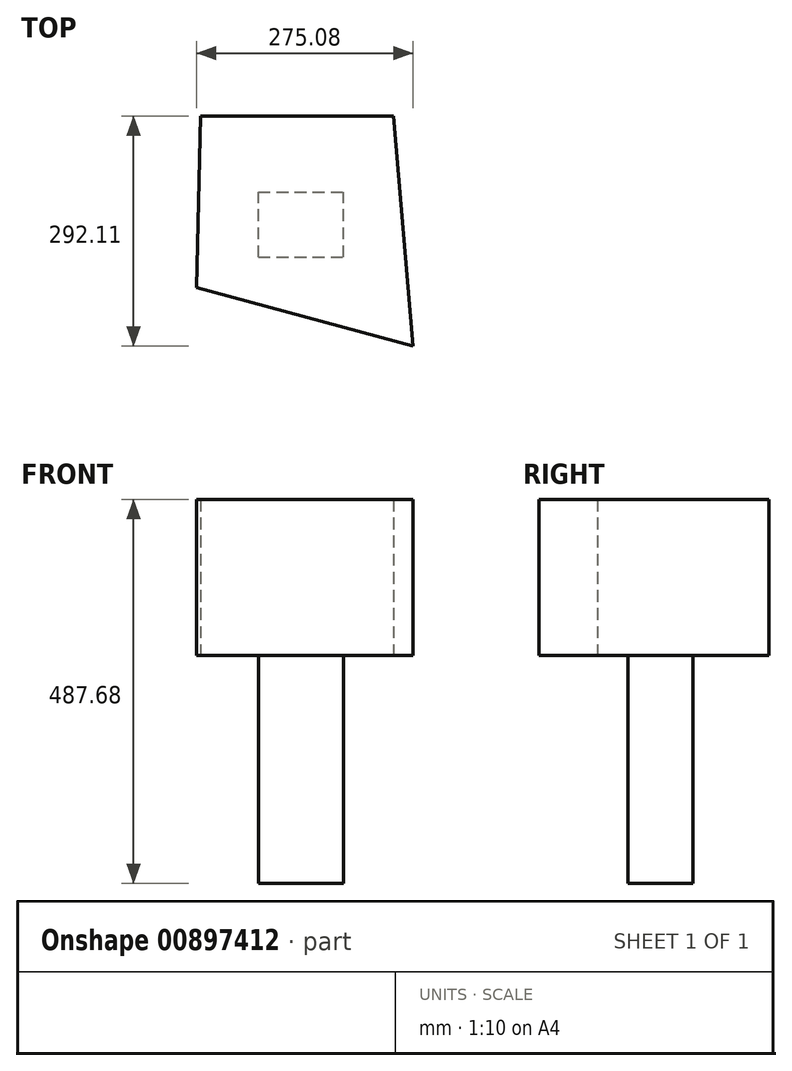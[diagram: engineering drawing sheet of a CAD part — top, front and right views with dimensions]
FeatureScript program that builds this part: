
annotation { "Feature Type Name" : "Feature", "Feature Type Description" : "" }
export const myFeature = defineFeature(function(context is Context, id is Id, definition is map)
    precondition{}
    {
        {
            var Q0;
            Q0=qCreatedBy(makeId("Top.planeOp"),FACE);
            var sketch = newSketch(context, id + "F0", { "sketchPlane" : qUnion([Q0])});
            skLineSegment(sketch, "E0", {"start": v(-124.73, -23.46) * mm, "end": v(150.35, -97.57) * mm});
            skLineSegment(sketch, "E1", {"start": v(150.35, -97.57) * mm, "end": v(125.82, 194.54) * mm});
            skLineSegment(sketch, "E2", {"start": v(125.82, 194.54) * mm, "end": v(-119.75, 194.54) * mm});
            skLineSegment(sketch, "E3", {"start": v(-119.75, 194.54) * mm, "end": v(-124.73, -23.46) * mm});
            skSolve(sketch);
        }
        {
            var Q0;
            Q0=makeQuery(id+"F0.imprint","IMPRINT",FACE,{"disambiguationData":[TD([[makeQuery(id+"F0.imprint","IMPRINT",EDGE,{"derivedFrom":sQuery(id+"F0.wireOp",EDGE,"E0")}),1.0]])]});
            extrude(context, id + "F1", {"entities" : qUnion([Q0]), "depth" : 198.12 * mm, "offsetDistance" : 25.4 * mm});
        }
        {
            var Q0;
            Q0=makeQuery(id+"F1.opExtrude","CAP_FACE",FACE,{"disambiguationData":[OSD([sQuery(id+"F0.wireOp",EDGE,"E0"),sQuery(id+"F0.wireOp",EDGE,"E1"),sQuery(id+"F0.wireOp",EDGE,"E2"),sQuery(id+"F0.wireOp",EDGE,"E3")])],"isStart":false});
            var sketch = newSketch(context, id + "F2", { "sketchPlane" : qUnion([Q0])});
            skLineSegment(sketch, "E4.bottom", {"start": v(-46.03, 15.18) * mm, "end": v(62.03, 15.18) * mm});
            skLineSegment(sketch, "E4.top", {"start": v(-46.03, 97.9) * mm, "end": v(62.03, 97.9) * mm});
            skLineSegment(sketch, "E4.left", {"start": v(-46.03, 15.18) * mm, "end": v(-46.03, 97.9) * mm});
            skLineSegment(sketch, "E4.right", {"start": v(62.03, 15.18) * mm, "end": v(62.03, 97.9) * mm});
            skSolve(sketch);
        }
        {
            var Q0;
            Q0=makeQuery(id+"F2.imprint","IMPRINT",FACE,{"disambiguationData":[TD([[makeQuery(id+"F2.imprint","IMPRINT",EDGE,{"derivedFrom":sQuery(id+"F2.wireOp",EDGE,"E4.bottom")}),1.0]])]});
            extrude(context, id + "F3", {"entities" : qUnion([Q0]), "operationType" : NewBodyOperationType.ADD, "oppositeDirection" : true, "depth" : 487.68 * mm, "offsetDistance" : 25.4 * mm});
        }
    });
